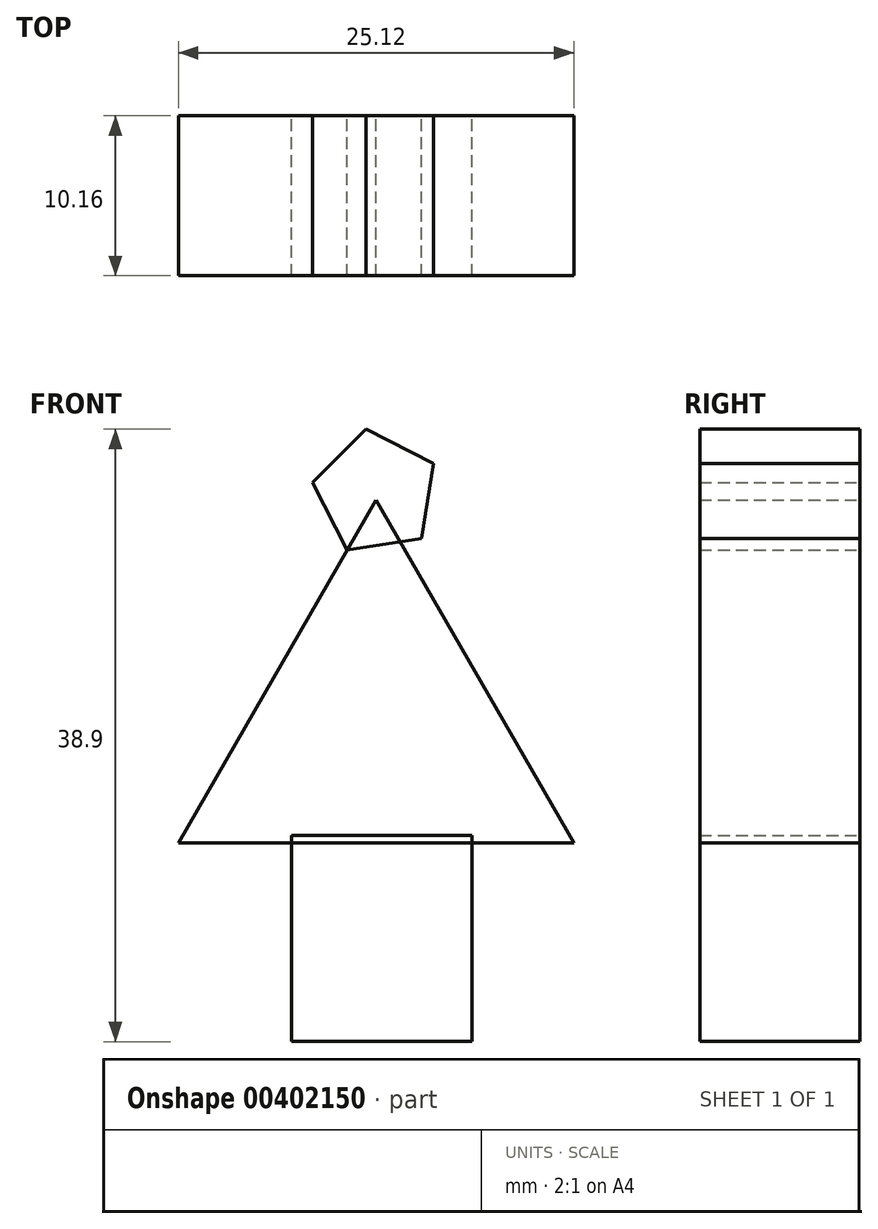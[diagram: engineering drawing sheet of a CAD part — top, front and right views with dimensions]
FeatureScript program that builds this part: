
annotation { "Feature Type Name" : "Feature", "Feature Type Description" : "" }
export const myFeature = defineFeature(function(context is Context, id is Id, definition is map)
    precondition{}
    {
        {
            var Q0;
            Q0=qCreatedBy(makeId("Front.planeOp"),FACE);
            var sketch = newSketch(context, id + "F0", { "sketchPlane" : qUnion([Q0])});
            skCircle(sketch, "E0.cCircle", {"center": v(0, 0) * mm, "radius": 7.25 * mm, "construction": true});
            skLineSegment(sketch, "E0.0", {"start": v(12.56, -7.25) * mm, "end": v(-12.56, -7.25) * mm});
            skLineSegment(sketch, "E0.1", {"start": v(-12.56, -7.25) * mm, "end": v(0, 14.5) * mm});
            skLineSegment(sketch, "E0.2", {"start": v(0, 14.5) * mm, "end": v(12.56, -7.25) * mm});
            skPoint(sketch, "E0.0.midPoint", {"position": v(0, -7.25) * mm});
            skSolve(sketch);
        }
        {
            var Q0;
            Q0=qCreatedBy(makeId("Front.planeOp"),FACE);
            var sketch = newSketch(context, id + "F1", { "sketchPlane" : qUnion([Q0])});
            skLineSegment(sketch, "E1.bottom", {"start": v(-5.38, -6.78) * mm, "end": v(6.08, -6.78) * mm});
            skLineSegment(sketch, "E1.top", {"start": v(-5.38, -19.89) * mm, "end": v(6.08, -19.89) * mm});
            skLineSegment(sketch, "E1.left", {"start": v(-5.38, -6.78) * mm, "end": v(-5.38, -19.89) * mm});
            skLineSegment(sketch, "E1.right", {"start": v(6.08, -6.78) * mm, "end": v(6.08, -19.89) * mm});
            skSolve(sketch);
        }
        {
            var Q0;
            Q0=qCreatedBy(makeId("Front.planeOp"),FACE);
            var sketch = newSketch(context, id + "F2", { "sketchPlane" : qUnion([Q0])});
            skCircle(sketch, "E2.cCircle", {"center": v(0, 14.97) * mm, "radius": 3.3 * mm, "construction": true});
            skLineSegment(sketch, "E2.0", {"start": v(-4.04, 15.61) * mm, "end": v(-0.64, 19.01) * mm});
            skLineSegment(sketch, "E2.1", {"start": v(-0.64, 19.01) * mm, "end": v(3.64, 16.83) * mm});
            skLineSegment(sketch, "E2.2", {"start": v(3.64, 16.83) * mm, "end": v(2.9, 12.08) * mm});
            skLineSegment(sketch, "E2.3", {"start": v(2.9, 12.08) * mm, "end": v(-1.86, 11.33) * mm});
            skLineSegment(sketch, "E2.4", {"start": v(-1.86, 11.33) * mm, "end": v(-4.04, 15.61) * mm});
            skPoint(sketch, "E2.0.midPoint", {"position": v(-2.34, 17.31) * mm});
            skSolve(sketch);
        }
        {
            var Q0;
            Q0 = qSketchRegion(id + "F1", true);
            var Q1;
            Q1 = qSketchRegion(id + "F2", true);
            var Q2;
            Q2 = qSketchRegion(id + "F0", true);
            extrude(context, id + "F3", {"entities" : qUnion([Q0, Q1, Q2]), "depth" : 10.16 * mm});
        }
    });
